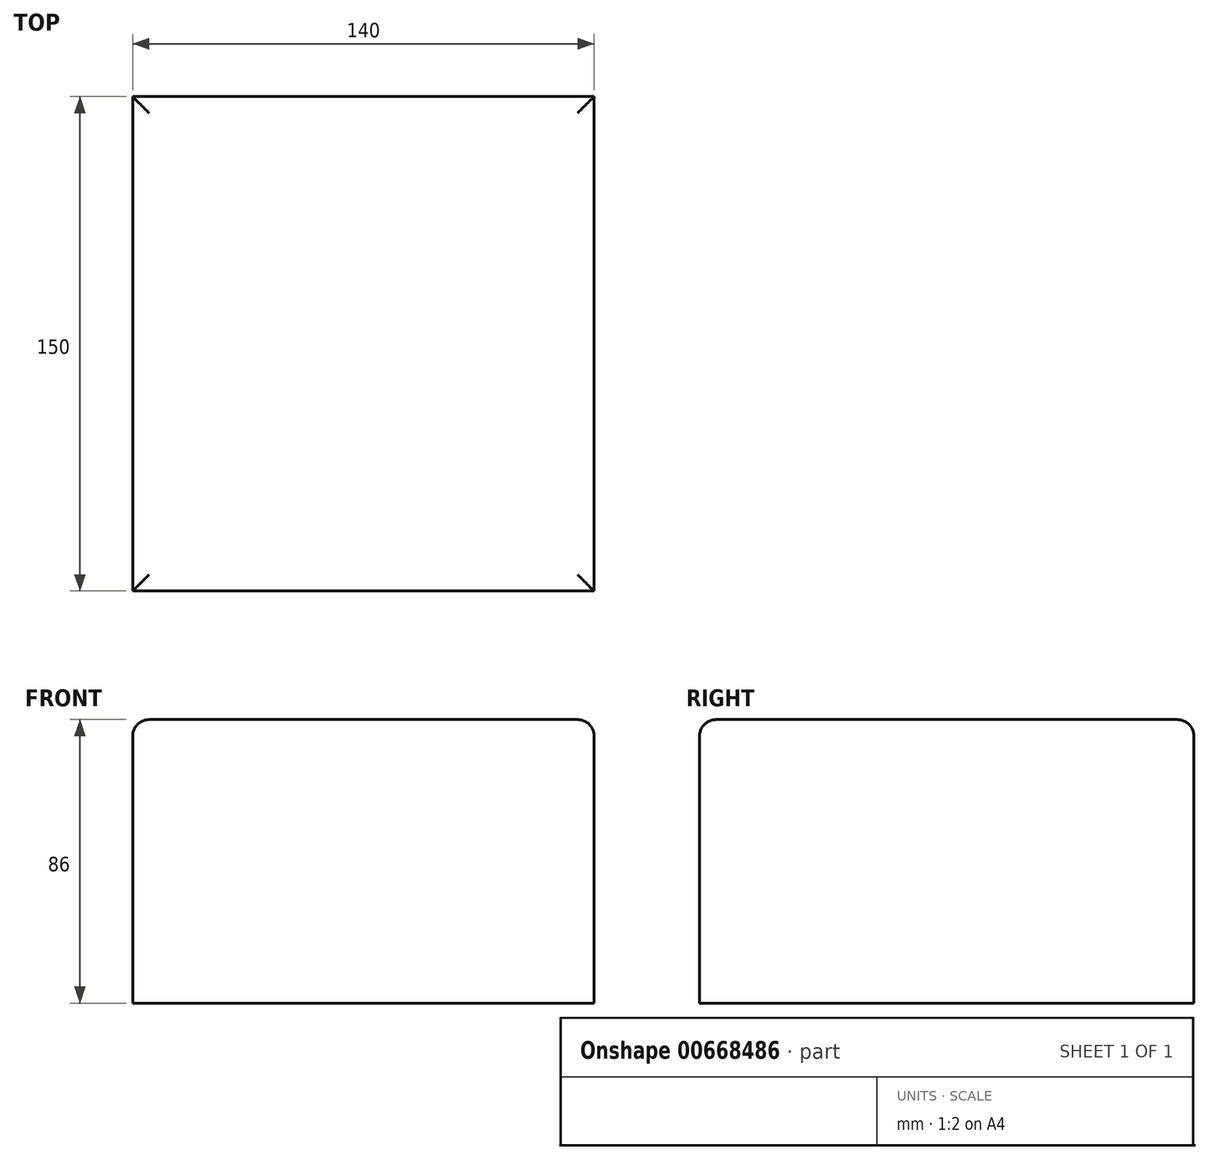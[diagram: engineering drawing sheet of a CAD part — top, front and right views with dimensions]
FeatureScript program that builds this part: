
annotation { "Feature Type Name" : "Feature", "Feature Type Description" : "" }
export const myFeature = defineFeature(function(context is Context, id is Id, definition is map)
    precondition{}
    {
        {
            var Q0;
            Q0=qCreatedBy(makeId("Top.planeOp"),FACE);
            var sketch = newSketch(context, id + "F0", { "sketchPlane" : qUnion([Q0])});
            skLineSegment(sketch, "E0.bottom", {"start": v(70, 75) * mm, "end": v(-70, 75) * mm});
            skLineSegment(sketch, "E0.top", {"start": v(70, -75) * mm, "end": v(-70, -75) * mm});
            skLineSegment(sketch, "E0.left", {"start": v(70, 75) * mm, "end": v(70, -75) * mm});
            skLineSegment(sketch, "E0.right", {"start": v(-70, 75) * mm, "end": v(-70, -75) * mm});
            skPoint(sketch, "E0.middle", {"position": v(0, 0) * mm});
            skSolve(sketch);
        }
        {
            var Q0;
            Q0=makeQuery(id+"F0.imprint","IMPRINT",FACE,{"disambiguationData":[TD([[makeQuery(id+"F0.imprint","IMPRINT",EDGE,{"derivedFrom":sQuery(id+"F0.wireOp",EDGE,"E0.bottom")}),1.0]])]});
            extrude(context, id + "F1", {"entities" : qUnion([Q0]), "depth" : 86 * mm, "offsetDistance" : 25 * mm});
        }
        {
            var Q0;
            Q0=makeQuery(id+"F1.opExtrude","CAP_EDGE",EDGE,{"disambiguationData":[OSD([sQuery(id+"F0.wireOp",EDGE,"E0.left")])],"isStart":false});
            var Q1;
            Q1=makeQuery(id+"F1.opExtrude","CAP_EDGE",EDGE,{"disambiguationData":[OSD([sQuery(id+"F0.wireOp",EDGE,"E0.top")])],"isStart":false});
            var Q2;
            Q2=makeQuery(id+"F1.opExtrude","CAP_EDGE",EDGE,{"disambiguationData":[OSD([sQuery(id+"F0.wireOp",EDGE,"E0.bottom")])],"isStart":false});
            var Q3;
            Q3=makeQuery(id+"F1.opExtrude","CAP_EDGE",EDGE,{"disambiguationData":[OSD([sQuery(id+"F0.wireOp",EDGE,"E0.right")])],"isStart":false});
            fillet(context, id + "F2", {"entities" : qUnion([Q0, Q1, Q2, Q3]), "radius" : 5 * mm, "tangentPropagation" : true, "allowEdgeOverflow" : false});
        }
    });
